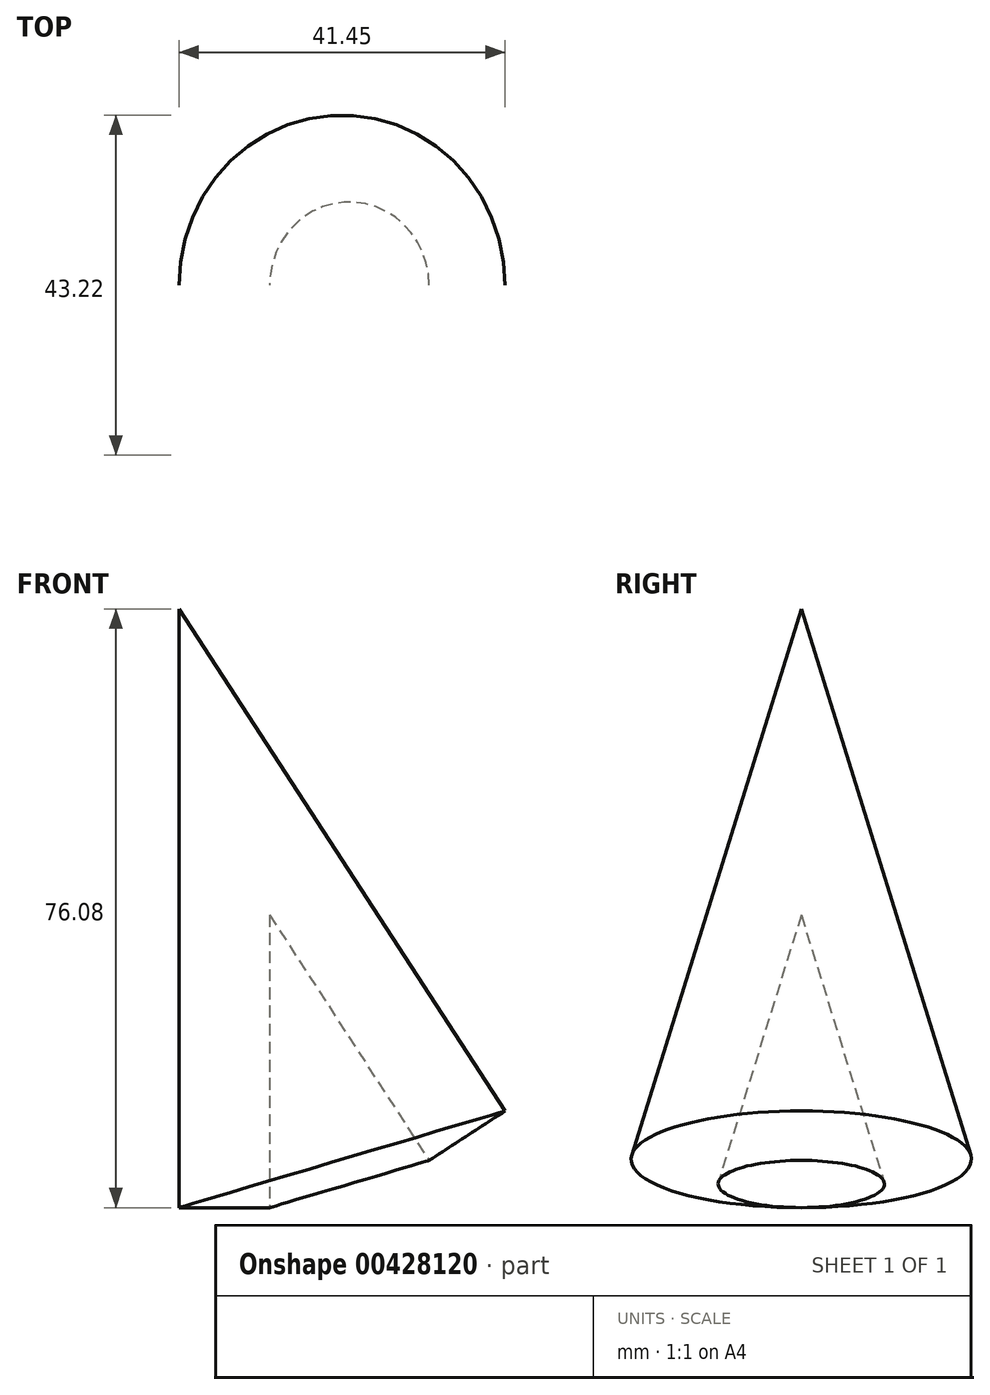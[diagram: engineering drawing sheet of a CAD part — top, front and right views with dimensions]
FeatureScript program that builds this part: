
annotation { "Feature Type Name" : "Feature", "Feature Type Description" : "" }
export const myFeature = defineFeature(function(context is Context, id is Id, definition is map)
    precondition{}
    {
        {
            var Q0;
            Q0=qCreatedBy(makeId("Front.planeOp"),FACE);
            var sketch = newSketch(context, id + "F0", { "sketchPlane" : qUnion([Q0])});
            skLineSegment(sketch, "E0", {"start": v(-62.5, 48.8) * mm, "end": v(-62.5, -27.28) * mm});
            skLineSegment(sketch, "E1", {"start": v(-50.97, 9.9) * mm, "end": v(-50.97, -27.28) * mm});
            skLineSegment(sketch, "E2", {"start": v(-50.97, -27.28) * mm, "end": v(-62.5, -27.28) * mm});
            skLineSegment(sketch, "E3", {"start": v(-62.5, 48.8) * mm, "end": v(-50.97, 9.9) * mm});
            skSolve(sketch);
        }
        {
            var Q0;
            Q0=makeQuery(id+"F0.imprint","IMPRINT",FACE,{"disambiguationData":[TD([[makeQuery(id+"F0.imprint","IMPRINT",EDGE,{"derivedFrom":sQuery(id+"F0.wireOp",EDGE,"E0")}),1.0]])]});
            var Q1;
            Q1=sQuery(id+"F0.wireOp",EDGE,"E3");
            revolve(context, id + "F1", {"entities" : qUnion([Q0]), "axis" : qUnion([Q1]), "revolveType" : RevolveType.FULL});
        }
    });
